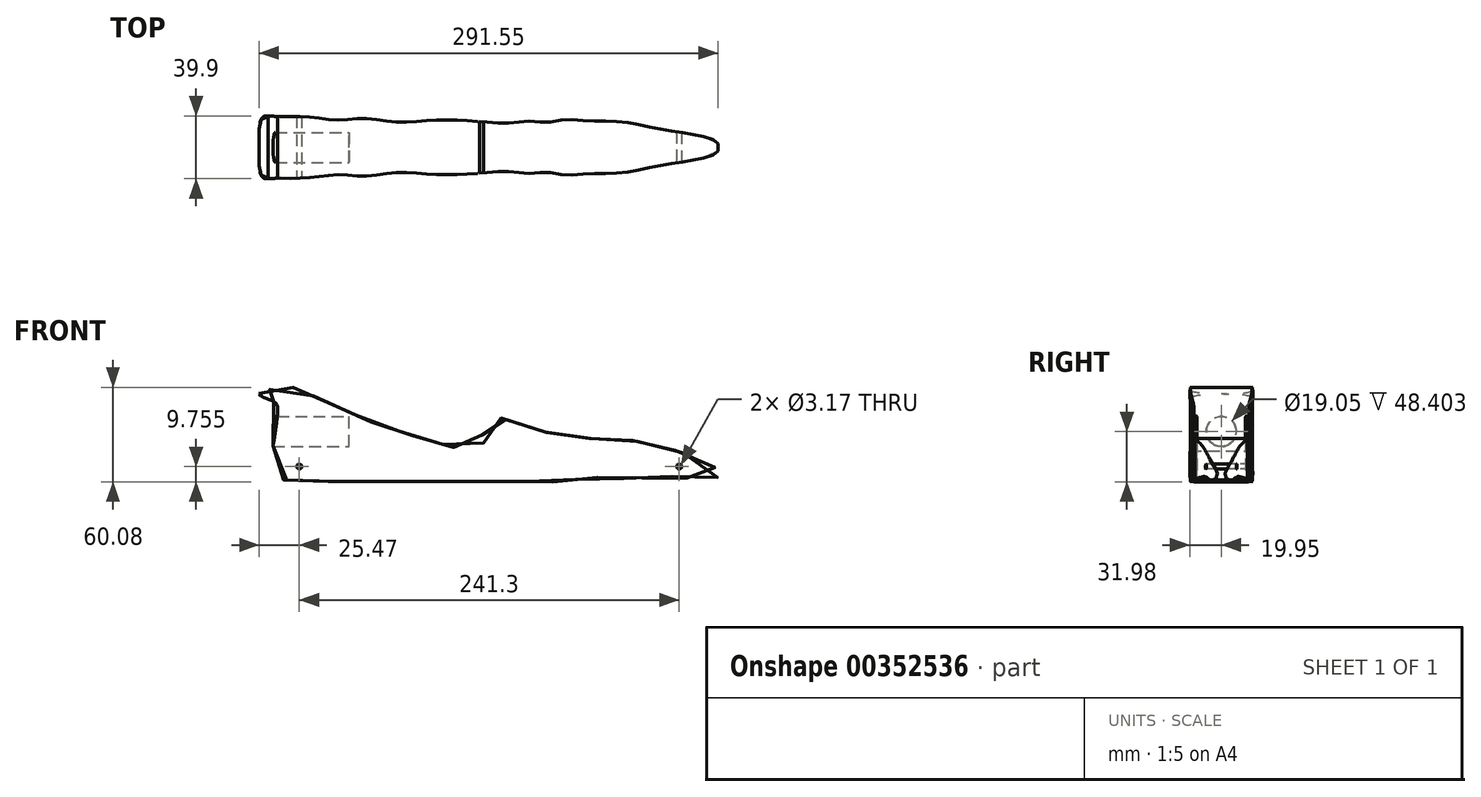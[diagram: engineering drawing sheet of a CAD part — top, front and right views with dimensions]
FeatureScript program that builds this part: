
annotation { "Feature Type Name" : "Feature", "Feature Type Description" : "" }
export const myFeature = defineFeature(function(context is Context, id is Id, definition is map)
    precondition{}
    {
        {
            var Q0;
            Q0=qCreatedBy(makeId("Front.planeOp"),FACE);
            var sketch = newSketch(context, id + "F0", { "sketchPlane" : qUnion([Q0])});
            skLineSegment(sketch, "E0.bottom", {"start": v(-146.05, 31.75) * mm, "end": v(146.05, 31.75) * mm, "construction": true});
            skLineSegment(sketch, "E0.top", {"start": v(-146.05, -31.75) * mm, "end": v(146.05, -31.75) * mm, "construction": true});
            skLineSegment(sketch, "E0.left", {"start": v(-146.05, 31.75) * mm, "end": v(-146.05, -31.75) * mm, "construction": true});
            skLineSegment(sketch, "E0.right", {"start": v(146.05, 31.75) * mm, "end": v(146.05, -31.75) * mm, "construction": true});
            skFitSpline(sketch, "E1", {"points": [v(-137.24, -9.12) * mm, v(-134.33, 14.6) * mm, v(-137.19, 19.25) * mm, v(-146.06, 23.56) * mm, v(-141.16, 26.34) * mm, v(-124.72, 28.06) * mm, v(-119.4, 26.15) * mm, v(-73.49, 5.42) * mm, v(-69.4, 4.01) * mm, v(-25, -9.3) * mm, v(-3.57, -9.3) * mm, v(-5.61, 8.1) * mm, v(18.92, 5.05) * mm, v(52.17, -3.69) * mm, v(81.14, -4.37) * mm, v(98.3, -7.32) * mm, v(143.7, -23.11) * mm, v(144.21, -30.1) * mm, v(139.18, -30.69) * mm, v(134.54, -30.6) * mm, v(124, -29.15) * mm, v(103.7, -28.87) * mm, v(87.43, -29.76) * mm, v(66.1, -29.1) * mm, v(47.16, -31.75) * mm, v(34.53, -31.75) * mm, v(9.26, -31.75) * mm, v(-6.9, -31.75) * mm, v(-33.35, -31.75) * mm, v(-67.27, -31.75) * mm, v(-87.28, -31.75) * mm, v(-110.16, -31.75) * mm, v(-139.12, -28.72) * mm, v(-140.25, -25.3) * mm, v(-138, -14.43) * mm, v(-137.24, -9.12) * mm]});
            skSolve(sketch);
        }
        {
            var Q0;
            Q0=qCreatedBy(makeId("Top.planeOp"),FACE);
            var sketch = newSketch(context, id + "F1", { "sketchPlane" : qUnion([Q0])});
            skLineSegment(sketch, "E2.bottom", {"start": v(-146.05, 22.22) * mm, "end": v(146.05, 22.23) * mm, "construction": true});
            skLineSegment(sketch, "E2.top", {"start": v(-146.05, -22.23) * mm, "end": v(146.05, -22.22) * mm, "construction": true});
            skLineSegment(sketch, "E2.left", {"start": v(-146.05, 22.22) * mm, "end": v(-146.05, -22.23) * mm, "construction": true});
            skLineSegment(sketch, "E2.right", {"start": v(146.05, 22.23) * mm, "end": v(146.05, -22.22) * mm, "construction": true});
            skLineSegment(sketch, "E3", {"start": v(-146.05, 0) * mm, "end": v(146.05, 0) * mm, "construction": true});
            skFitSpline(sketch, "E4", {"points": [v(-146.05, 0) * mm, v(-146.05, 12.35) * mm, v(-143.65, 19.23) * mm, v(-137.5, 19.74) * mm, v(-117.47, 19.49) * mm, v(-96.43, 17.43) * mm, v(-78.72, 18.2) * mm, v(-57.16, 15.9) * mm, v(-37.14, 17.18) * mm, v(-6.08, 16.4) * mm, v(10.09, 15.38) * mm, v(27.29, 16.66) * mm, v(36.53, 15.9) * mm, v(47.98, 17.6) * mm, v(62.32, 16.73) * mm, v(85.06, 16.2) * mm, v(102.68, 12.63) * mm, v(119.95, 9.83) * mm, v(134.4, 7.24) * mm, v(146.05, 0) * mm], "startDerivative": vector(0, 335.54) * mm, "endDerivative": vector(0, -277.49) * mm});
            skFitSpline(sketch, "E5.MirrorCS", {"points": [v(-146.05, 0) * mm, v(-146.05, -12.35) * mm, v(-143.65, -19.23) * mm, v(-137.5, -19.74) * mm, v(-117.47, -19.49) * mm, v(-96.43, -17.43) * mm, v(-78.72, -18.2) * mm, v(-57.16, -15.9) * mm, v(-37.14, -17.18) * mm, v(-6.08, -16.4) * mm, v(10.09, -15.38) * mm, v(27.29, -16.66) * mm, v(36.53, -15.9) * mm, v(47.98, -17.6) * mm, v(62.32, -16.73) * mm, v(85.06, -16.2) * mm, v(102.68, -12.63) * mm, v(119.95, -9.83) * mm, v(134.4, -7.24) * mm, v(146.05, 0) * mm], "startDerivative": vector(0, -335.54) * mm, "endDerivative": vector(0, 277.49) * mm});
            skLineSegment(sketch, "E6.MirrorCS", {"start": v(-146.05, -22.23) * mm, "end": v(146.05, -22.22) * mm});
            skSolve(sketch);
        }
        {
            var Q0;
            Q0=qCreatedBy(makeId("Right.planeOp"),FACE);
            var sketch = newSketch(context, id + "F2", { "sketchPlane" : qUnion([Q0])});
            skCircle(sketch, "E7", {"center": v(0, 0) * mm, "radius": 9.53 * mm});
            skSolve(sketch);
        }
        {
            var Q0;
            Q0=qCreatedBy(makeId("Front.planeOp"),FACE);
            var sketch = newSketch(context, id + "F3", { "sketchPlane" : qUnion([Q0])});
            skCircle(sketch, "E8", {"center": v(-120.65, -22.22) * mm, "radius": 1.59 * mm});
            skCircle(sketch, "E9", {"center": v(120.65, -22.23) * mm, "radius": 1.59 * mm});
            skSolve(sketch);
        }
        {
            var Q0;
            Q0=qSketchRegion(id+"F0",true);
            extrude(context, id + "F4", {"entities" : qUnion([Q0]), "depth" : 44.45 * mm, "symmetric" : true});
        }
        {
            var Q0;
            Q0=makeQuery(id+"F1.imprint","IMPRINT",FACE,{"disambiguationData":[TD([[makeQuery(id+"F1.imprint","IMPRINT",EDGE,{"derivedFrom":sQuery(id+"F1.wireOp",EDGE,"E4")}),-1.0]])]});
            var Q1;
            Q1=sQuery(id+"F1.wireOp",EDGE,"E5.MirrorCS");
            var Q2;
            Q2=sQuery(id+"F1.wireOp",EDGE,"E4");
            extrude(context, id + "F5", {"entities" : qUnion([Q0]), "operationType" : NewBodyOperationType.INTERSECT, "surfaceEntities" : qUnion([Q1, Q2]), "endBound" : BoundingType.THROUGH_ALL, "oppositeDirection" : true, "depth" : 31.75 * mm, "hasSecondDirection" : true, "secondDirectionBound" : BoundingType.THROUGH_ALL, "secondDirectionOppositeDirection" : false, "secondDirectionDepth" : 25.4 * mm});
        }
        {
            var Q0;
            Q0=qSketchRegion(id+"F2",true);
            extrude(context, id + "F6", {"entities" : qUnion([Q0]), "operationType" : NewBodyOperationType.REMOVE, "oppositeDirection" : true, "depth" : 152.4 * mm, "hasSecondDirection" : true, "secondDirectionOppositeDirection" : true, "secondDirectionDepth" : 88.9 * mm});
        }
        {
            var Q0;
            Q0=qSketchRegion(id+"F3",true);
            extrude(context, id + "F7", {"entities" : qUnion([Q0]), "operationType" : NewBodyOperationType.REMOVE, "oppositeDirection" : true, "depth" : 50.8 * mm, "symmetric" : true});
        }
    });
